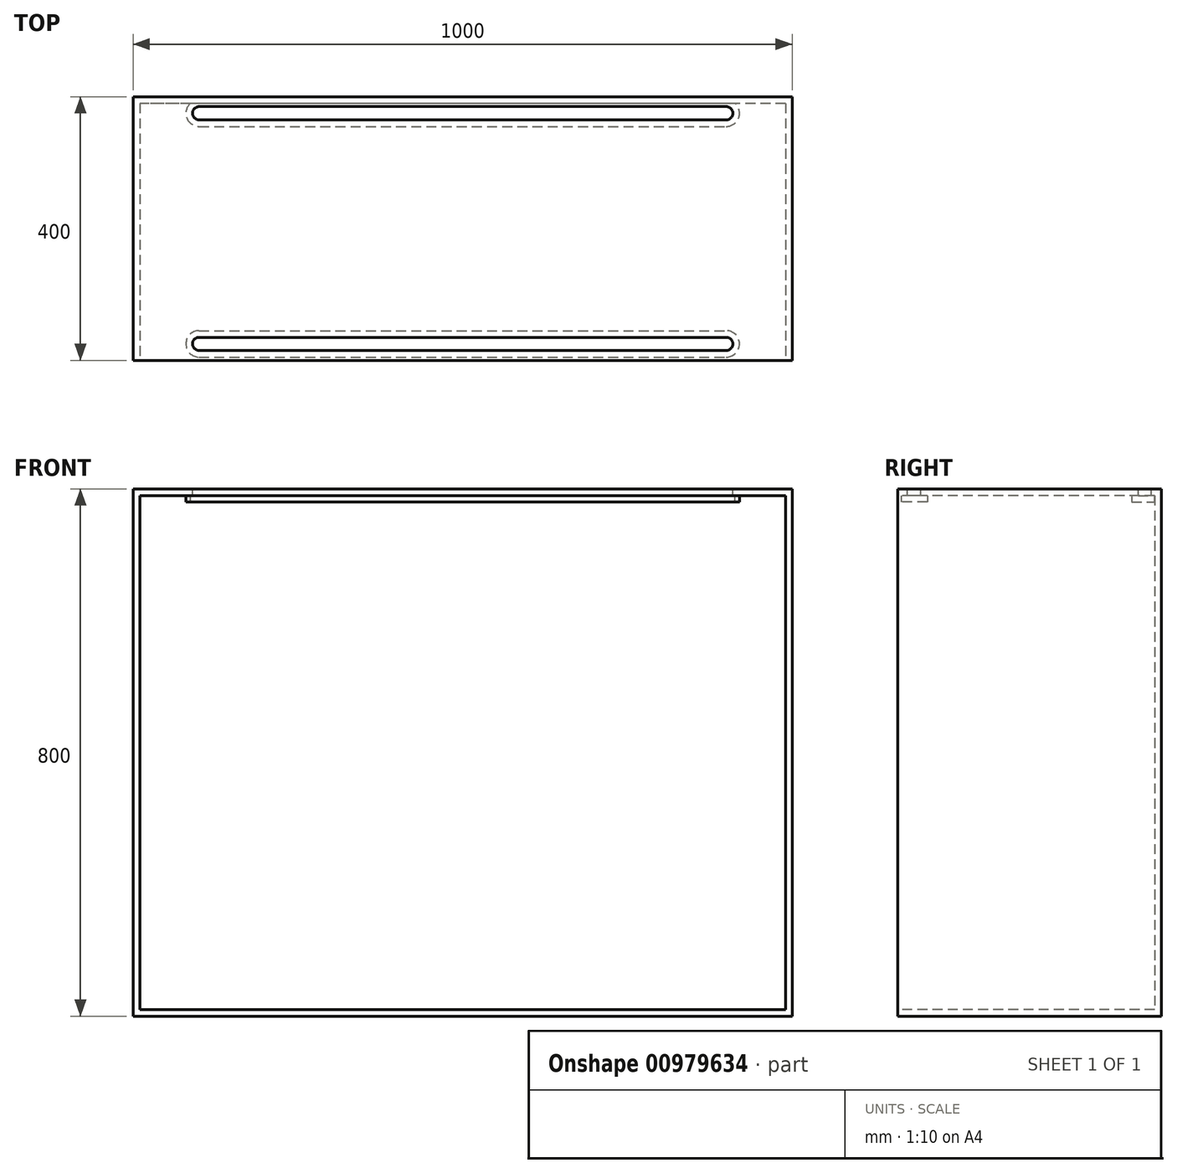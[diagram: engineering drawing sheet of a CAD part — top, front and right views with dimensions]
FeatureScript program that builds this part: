
annotation { "Feature Type Name" : "Feature", "Feature Type Description" : "" }
export const myFeature = defineFeature(function(context is Context, id is Id, definition is map)
    precondition{}
    {
        {
            var Q0;
            Q0=qCreatedBy(makeId("Front.planeOp"),FACE);
            var sketch = newSketch(context, id + "F0", { "sketchPlane" : qUnion([Q0])});
            skLineSegment(sketch, "E0.bottom", {"start": v(500, 400) * mm, "end": v(-500, 400) * mm});
            skLineSegment(sketch, "E0.top", {"start": v(500, -400) * mm, "end": v(-500, -400) * mm});
            skLineSegment(sketch, "E0.left", {"start": v(500, 400) * mm, "end": v(500, -400) * mm});
            skLineSegment(sketch, "E0.right", {"start": v(-500, 400) * mm, "end": v(-500, -400) * mm});
            skPoint(sketch, "E0.middle", {"position": v(0, 0) * mm});
            skSolve(sketch);
        }
        {
            var Q0;
            Q0=makeQuery(id+"F0.imprint","IMPRINT",FACE,{"disambiguationData":[TD([[makeQuery(id+"F0.imprint","IMPRINT",EDGE,{"derivedFrom":sQuery(id+"F0.wireOp",EDGE,"E0.bottom")}),1.0]])]});
            extrude(context, id + "F1", {"entities" : qUnion([Q0]), "oppositeDirection" : true, "depth" : 400 * mm, "offsetDistance" : 25 * mm});
        }
        {
            var Q0;
            Q0=makeQuery(id+"F1.opExtrude","SWEPT_FACE",FACE,{"disambiguationData":[OSD([sQuery(id+"F0.wireOp",EDGE,"E0.bottom")])]});
            var sketch = newSketch(context, id + "F2", { "sketchPlane" : qUnion([Q0])});
            skLineSegment(sketch, "E1", {"start": v(0, 400) * mm, "end": v(0, 0) * mm, "construction": true});
            skLineSegment(sketch, "E2", {"start": v(-400, 25) * mm, "end": v(400, 25) * mm, "construction": true});
            skLineSegment(sketch, "E3", {"start": v(0, 200) * mm, "end": v(500, 200) * mm, "construction": true});
            skPoint(sketch, "E4", {"position": v(0, 25) * mm});
            skArc(sketch, "E5.0.startCap", {"start": v(-400, 15) * mm, "mid": v(-410, 25) * mm, "end": v(-400, 35) * mm});
            skArc(sketch, "E5.0.endCap", {"start": v(400, 35) * mm, "mid": v(410, 25) * mm, "end": v(400, 15) * mm});
            skLineSegment(sketch, "E5.0.left", {"start": v(-400, 35) * mm, "end": v(400, 35) * mm});
            skLineSegment(sketch, "E5.0.right", {"start": v(-400, 15) * mm, "end": v(400, 15) * mm});
            skArc(sketch, "E6.MirrorCS", {"start": v(400, 365) * mm, "mid": v(410, 375) * mm, "end": v(400, 385) * mm});
            skLineSegment(sketch, "E7.MirrorCS", {"start": v(-400, 385) * mm, "end": v(400, 385) * mm});
            skLineSegment(sketch, "E8.MirrorCS", {"start": v(-400, 365) * mm, "end": v(400, 365) * mm});
            skArc(sketch, "E9.MirrorCS", {"start": v(-400, 385) * mm, "mid": v(-410, 375) * mm, "end": v(-400, 365) * mm});
            skSolve(sketch);
        }
        {
            var Q0;
            Q0 = qSketchRegion(id + "F2", true);
            extrude(context, id + "F3", {"entities" : qUnion([Q0]), "operationType" : NewBodyOperationType.REMOVE, "oppositeDirection" : true, "depth" : 10 * mm, "offsetDistance" : 25 * mm});
        }
        {
            var Q0;
            Q0=makeQuery(id+"F1.opExtrude","CAP_FACE",FACE,{"disambiguationData":[OSD([sQuery(id+"F0.wireOp",EDGE,"E0.bottom"),sQuery(id+"F0.wireOp",EDGE,"E0.top"),sQuery(id+"F0.wireOp",EDGE,"E0.left"),sQuery(id+"F0.wireOp",EDGE,"E0.right")])],"isStart":true});
            shell(context, id + "F4", {"entities" : qUnion([Q0]), "thickness" : 10 * mm});
        }
    });
